# Revit family: Sanitary_Toilets_Toto_CST776CEFG-Drake-2pc-Toilet
name_source: partatom
category: Plumbing Fixtures
units: mm (PartAtom-declared; Revit-internal decimal feet)

## family parameters
Cut with Voids When Loaded = No
Host = Face
OmniClass Number = 23.45.05.21.11
OmniClass Title = Water Closets
Part Type = Normal
Room Calculation Point = No
Round Connector Dimension = Use Diameter
Shared = No

## types (2) — shared parameters
Assembly Code = D2010
Cold Water Inlet Connection Diameter = 1"
Default Elevation = 0"
Depth = 28 3/8"
Description = Drake 2pc Toilet (tank and bowl)
Edition number = 1
Flush Lever Finish = Toto - Chrome - Polished
Height = 16 1/8"
Keynote = 15410
Manufacturer = TOTO USA Inc.
Maximum Pressure (static) = 80.00 psi
Minimum Water Pressure (flowing) = 8.00 psi
Model = CST776CEFG
Product Material = Toto - Vitreous China - Cotton
Sanitary Drain Connection Diameter = 2"
URL = http://www.totousa.com
Weight = 94.00 lb
Width = 14"
zero-valued in all types: CWFU, WFU

## per-type parameters (varying)
| type | Flush Rate |
| CST776CEFG | 1.28 GPF |
| CST776CSFG | 1.6 GPF |

## geometry (parser evidence)
native form markers: Sweep x5
no freeform markers — native parametric forms only
